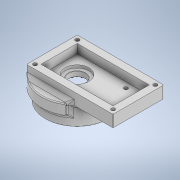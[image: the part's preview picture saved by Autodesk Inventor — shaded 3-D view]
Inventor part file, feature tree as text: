
AUTODESK INVENTOR PART (.ipt)
format: ipt  version: 2022 (Build 260153000, 153)  size: 779,776 bytes
history: native  units: mm
features: extrude x12, sketch x12, fillet x11, projected_geometry x3, other x2, pattern_circular x1
ambient origin geometry x8: Origin, YZ Plane, XZ Plane, XY Plane, X Axis, Y Axis, Z Axis, Center Point
bodies: Body1 (feature_tree)
feature tree (41):
  other  "Твердое тело1"
  extrude  "Выдавливание1"  Depth=20.0mm
  extrude  "Выдавливание3"  Depth=39.7mm
  extrude  "Выдавливание4"  Depth=4.0mm
  extrude  "Выдавливание6"  Depth=4.0mm
  extrude  "Выдавливание8"  Depth=5.0mm TaperAngle=0.0deg
  extrude  "Выдавливание9"  Depth=13.2mm
  fillet  "Сопряжение1"  Radius=9.8mm
  extrude  "Выдавливание10"  Depth=16.6mm
  extrude  "Выдавливание12"  Depth=8.0mm
  fillet  "Сопряжение4"  Radius=2.1mm
  fillet  "Сопряжение5"  Radius=13.22mm
  fillet  "Сопряжение6"  Radius=7.0mm
  fillet  "Сопряжение7"  Radius=7.0mm
  extrude  "Выдавливание15"  Depth=1.5mm TaperAngle=0.0deg
  fillet  "Сопряжение8"  Radius=2.1mm
  other  "РабОсь1"
  pattern_circular  "Круговой массив1"  Count=10  [1 undecoded]
  fillet  "Сопряжение9"  Radius=9.2mm
  fillet  "Сопряжение11"  Radius=35.0mm
  fillet  "Сопряжение12"  Radius=2.9mm
  fillet  "Сопряжение13"  Radius=20.0mm
  extrude  "Выдавливание16"  Depth=2.1mm TaperAngle=0.0deg
  extrude  "Выдавливание17"  Depth=2.0mm
  extrude  "Выдавливание18"  Depth=6.0mm TaperAngle=0.0deg
  fillet  "Сопряжение15"  Radius=2.0mm
  sketch  "Эскиз1"
  sketch  "Эскиз2"
  sketch  "Эскиз3"
  projected_geometry  "Спроецированная петля1"
  sketch  "Эскиз4"
  projected_geometry  "Спроецированная петля2"
  sketch  "Эскиз6"
  projected_geometry  "Спроецированная петля3"
  sketch  "Эскиз7"
  sketch  "Эскиз8"
  sketch  "Эскиз9"
  sketch  "Эскиз12"
  sketch  "Эскиз13"
  sketch  "Эскиз14"
  sketch  "Эскиз15"
note: 1 required parameter value undecoded (feature->parameter linkage not recoverable at this tier; creation-order binding heuristic only, values carry confidence <= 0.55)
